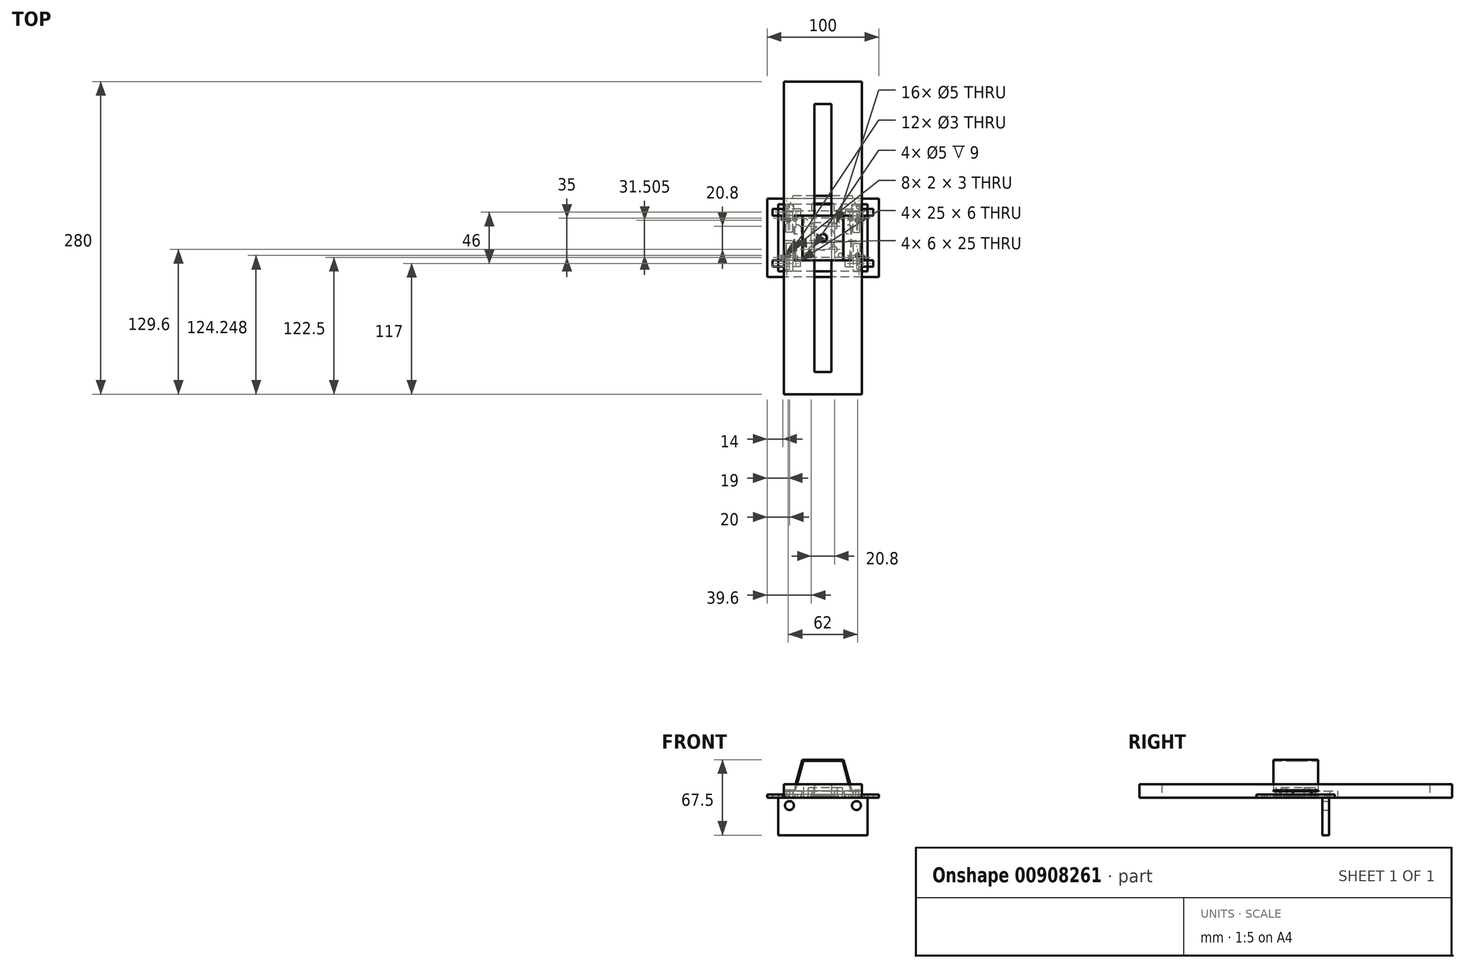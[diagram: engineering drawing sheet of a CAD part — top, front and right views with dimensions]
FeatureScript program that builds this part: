
annotation { "Feature Type Name" : "Feature", "Feature Type Description" : "" }
export const myFeature = defineFeature(function(context is Context, id is Id, definition is map)
    precondition{}
    {
        {
            var Q0;
            Q0=qCreatedBy(makeId("Top.planeOp"),FACE);
            var sketch = newSketch(context, id + "F0", { "sketchPlane" : qUnion([Q0])});
            skLineSegment(sketch, "E0.bottom", {"start": v(40, 30) * mm, "end": v(-40, 30) * mm});
            skLineSegment(sketch, "E0.top", {"start": v(40, -30) * mm, "end": v(-40, -30) * mm});
            skLineSegment(sketch, "E0.left", {"start": v(40, 30) * mm, "end": v(40, -30) * mm});
            skLineSegment(sketch, "E0.right", {"start": v(-40, 30) * mm, "end": v(-40, -30) * mm});
            skPoint(sketch, "E0.middle", {"position": v(0, 0) * mm});
            skCircle(sketch, "E1", {"center": v(0, 0) * mm, "radius": 4.5 * mm});
            skCircle(sketch, "E2", {"center": v(15.5, 15.5) * mm, "radius": 1.75 * mm});
            skCircle(sketch, "E3.MirrorC", {"center": v(-15.5, 15.5) * mm, "radius": 1.75 * mm});
            skCircle(sketch, "E4.MirrorC", {"center": v(-15.5, -15.5) * mm, "radius": 1.75 * mm});
            skCircle(sketch, "E5.MirrorC", {"center": v(15.5, -15.5) * mm, "radius": 1.75 * mm});
            skSolve(sketch);
        }
        {
            var Q0;
            Q0 = qSketchRegion(id + "F0", true);
            extrude(context, id + "F1", {"entities" : qUnion([Q0]), "depth" : 3 * mm, "offsetDistance" : 25 * mm});
        }
        {
            var Q0;
            Q0=makeQuery(id+"F1.opExtrude","CAP_FACE",FACE,{"disambiguationData":[OSD([sQuery(id+"F0.wireOp",EDGE,"E0.bottom"),sQuery(id+"F0.wireOp",EDGE,"E0.top"),sQuery(id+"F0.wireOp",EDGE,"E0.left"),sQuery(id+"F0.wireOp",EDGE,"E0.right"),sQuery(id+"F0.wireOp",EDGE,"E1"),sQuery(id+"F0.wireOp",EDGE,"E2"),sQuery(id+"F0.wireOp",EDGE,"6a0f09f9-d6d8-4e83-8fd7-3011a86620b10.MirrorC"),sQuery(id+"F0.wireOp",EDGE,"6c786a74-0100-4ea5-b8c0-d8c8957705b30.MirrorC"),sQuery(id+"F0.wireOp",EDGE,"6c786a74-0100-4ea5-b8c0-d8c8957705b31.MirrorC")])],"isStart":true});
            var sketch = newSketch(context, id + "F2", { "sketchPlane" : qUnion([Q0])});
            skLineSegment(sketch, "E6.bottom", {"start": v(40, -30) * mm, "end": v(-40, -30) * mm});
            skLineSegment(sketch, "E6.top", {"start": v(40, -24) * mm, "end": v(-40, -24) * mm});
            skLineSegment(sketch, "E6.left", {"start": v(40, -30) * mm, "end": v(40, -24) * mm});
            skLineSegment(sketch, "E6.right", {"start": v(-40, -30) * mm, "end": v(-40, -24) * mm});
            skSolve(sketch);
        }
        {
            var Q0;
            Q0 = qSketchRegion(id + "F2", true);
            extrude(context, id + "F3", {"entities" : qUnion([Q0]), "depth" : 33.5 * mm, "offsetDistance" : 25 * mm});
        }
        {
            var Q0;
            Q0=qCreatedBy(makeId("Top.planeOp"),FACE);
            var sketch = newSketch(context, id + "F4", { "sketchPlane" : qUnion([Q0])});
            skLineSegment(sketch, "E7.bottom", {"start": v(35, 140) * mm, "end": v(-35, 140) * mm});
            skLineSegment(sketch, "E7.top", {"start": v(35, -140) * mm, "end": v(-35, -140) * mm});
            skLineSegment(sketch, "E7.left", {"start": v(35, 140) * mm, "end": v(35, -140) * mm});
            skLineSegment(sketch, "E7.right", {"start": v(-35, 140) * mm, "end": v(-35, -140) * mm});
            skPoint(sketch, "E7.middle", {"position": v(0, 0) * mm});
            skLineSegment(sketch, "E8.bottom", {"start": v(-7.5, 120) * mm, "end": v(7.5, 120) * mm});
            skLineSegment(sketch, "E8.top", {"start": v(-7.5, -120) * mm, "end": v(7.5, -120) * mm});
            skLineSegment(sketch, "E8.left", {"start": v(-7.5, 120) * mm, "end": v(-7.5, -120) * mm});
            skLineSegment(sketch, "E8.right", {"start": v(7.5, 120) * mm, "end": v(7.5, -120) * mm});
            skSolve(sketch);
        }
        {
            var Q0;
            Q0=makeQuery(id+"F4.imprint","IMPRINT",FACE,{"disambiguationData":[TD([[makeQuery(id+"F4.imprint","IMPRINT",EDGE,{"derivedFrom":sQuery(id+"F4.wireOp",EDGE,"E7.bottom")}),1.0]])]});
            extrude(context, id + "F5", {"entities" : qUnion([Q0]), "depth" : 12 * mm, "offsetDistance" : 25 * mm});
        }
        {
            var Q0;
            Q0=makeQuery(id+"F1.opExtrude","CAP_FACE",FACE,{"disambiguationData":[OSD([sQuery(id+"F0.wireOp",EDGE,"E0.bottom"),sQuery(id+"F0.wireOp",EDGE,"E0.top"),sQuery(id+"F0.wireOp",EDGE,"E0.left"),sQuery(id+"F0.wireOp",EDGE,"E0.right"),sQuery(id+"F0.wireOp",EDGE,"E1"),sQuery(id+"F0.wireOp",EDGE,"E2"),sQuery(id+"F0.wireOp",EDGE,"6a0f09f9-d6d8-4e83-8fd7-3011a86620b10.MirrorC"),sQuery(id+"F0.wireOp",EDGE,"6c786a74-0100-4ea5-b8c0-d8c8957705b30.MirrorC"),sQuery(id+"F0.wireOp",EDGE,"6c786a74-0100-4ea5-b8c0-d8c8957705b31.MirrorC")])],"isStart":true});
            var sketch = newSketch(context, id + "F6", { "sketchPlane" : qUnion([Q0])});
            skCircle(sketch, "E9", {"center": v(0, 0) * mm, "radius": 11 * mm});
            skSolve(sketch);
        }
        {
            var Q0;
            Q0 = qSketchRegion(id + "F6", true);
            extrude(context, id + "F7", {"entities" : qUnion([Q0]), "operationType" : NewBodyOperationType.REMOVE, "oppositeDirection" : true, "depth" : 2 * mm, "offsetDistance" : 25 * mm});
        }
        {
            var Q0;
            Q0=makeQuery(id+"F3.boolean.opBoolean","MERGE",FACE,{"derivedFrom":[makeQuery(id+"F1.opExtrude","SWEPT_FACE",FACE,{"disambiguationData":[OSD([sQuery(id+"F0.wireOp",EDGE,"E0.bottom")])]}),makeQuery(id+"F3.opExtrude","SWEPT_FACE",FACE,{"disambiguationData":[OSD([sQuery(id+"F2.wireOp",EDGE,"E6.bottom")])]})]});
            var sketch = newSketch(context, id + "F8", { "sketchPlane" : qUnion([Q0])});
            skCircle(sketch, "E10", {"center": v(-30, -7) * mm, "radius": 4 * mm});
            skCircle(sketch, "E11.MirrorC", {"center": v(30, -7) * mm, "radius": 4 * mm});
            skSolve(sketch);
        }
        {
            var Q0;
            Q0 = qSketchRegion(id + "F8", true);
            extrude(context, id + "F9", {"entities" : qUnion([Q0]), "operationType" : NewBodyOperationType.REMOVE, "oppositeDirection" : true, "depth" : 6 * mm, "offsetDistance" : 25 * mm});
        }
        {
            var Q0;
            Q0=qCreatedBy(makeId("Front.planeOp"),FACE);
            var sketch = newSketch(context, id + "F10", { "sketchPlane" : qUnion([Q0])});
            skLineSegment(sketch, "E12", {"start": v(0, 33) * mm, "end": v(-17.63, 33) * mm});
            skLineSegment(sketch, "E13", {"start": v(-17.63, 33) * mm, "end": v(-25, 5.62) * mm});
            skLineSegment(sketch, "E14", {"start": v(-25, 5.62) * mm, "end": v(-35, 5.62) * mm});
            skLineSegment(sketch, "E15.0", {"start": v(-25.77, 6.62) * mm, "end": v(-35, 6.62) * mm});
            skLineSegment(sketch, "E15.1", {"start": v(-18.4, 34) * mm, "end": v(-25.77, 6.62) * mm});
            skLineSegment(sketch, "E15.2", {"start": v(0, 34) * mm, "end": v(-18.4, 34) * mm});
            skLineSegment(sketch, "E16", {"start": v(-35, 6.62) * mm, "end": v(-35, 5.62) * mm});
            skLineSegment(sketch, "E17.MirrorCS", {"start": v(35, 6.62) * mm, "end": v(35, 5.62) * mm});
            skLineSegment(sketch, "E18.MirrorCS", {"start": v(25, 5.62) * mm, "end": v(35, 5.62) * mm});
            skLineSegment(sketch, "E19.MirrorCS", {"start": v(25.77, 6.62) * mm, "end": v(35, 6.62) * mm});
            skLineSegment(sketch, "E20.MirrorCS", {"start": v(18.4, 34) * mm, "end": v(25.77, 6.62) * mm});
            skLineSegment(sketch, "E21.MirrorCS", {"start": v(17.63, 33) * mm, "end": v(25, 5.62) * mm});
            skLineSegment(sketch, "E22.MirrorCS", {"start": v(0, 34) * mm, "end": v(18.4, 34) * mm});
            skLineSegment(sketch, "E23.MirrorCS", {"start": v(0, 33) * mm, "end": v(17.63, 33) * mm});
            skSolve(sketch);
        }
        {
            var Q0;
            Q0 = qSketchRegion(id + "F10", true);
            extrude(context, id + "F11", {"entities" : qUnion([Q0]), "depth" : 20 * mm, "offsetDistance" : 25 * mm, "hasSecondDirection" : true, "secondDirectionOppositeDirection" : true, "secondDirectionDepth" : 20 * mm});
        }
        {
            var Q0;
            Q0=qCreatedBy(makeId("Top.planeOp"),FACE);
            var sketch = newSketch(context, id + "F12", { "sketchPlane" : qUnion([Q0])});
            skCircle(sketch, "E24", {"center": v(-31, 15.75) * mm, "radius": 1.5 * mm});
            skCircle(sketch, "E25.MirrorC", {"center": v(31, 15.75) * mm, "radius": 1.5 * mm});
            skCircle(sketch, "E26.MirrorC", {"center": v(31, -15.75) * mm, "radius": 1.5 * mm});
            skCircle(sketch, "E27.MirrorC", {"center": v(-31, -15.75) * mm, "radius": 1.5 * mm});
            skSolve(sketch);
        }
        {
            var Q0;
            Q0 = qSketchRegion(id + "F12", true);
            extrude(context, id + "F13", {"entities" : qUnion([Q0]), "operationType" : NewBodyOperationType.REMOVE, "oppositeDirection" : true, "depth" : 25 * mm, "offsetDistance" : 25 * mm, "hasSecondDirection" : true, "secondDirectionOppositeDirection" : false, "secondDirectionDepth" : 25 * mm});
        }
        {
            var Q0;
            Q0=qCreatedBy(makeId("Top.planeOp"),FACE);
            var sketch = newSketch(context, id + "F14", { "sketchPlane" : qUnion([Q0])});
            skCircle(sketch, "E28", {"center": v(0, 0) * mm, "radius": 3.3 * mm});
            skSolve(sketch);
        }
        {
            var Q0;
            Q0 = qSketchRegion(id + "F14", true);
            extrude(context, id + "F15", {"entities" : qUnion([Q0]), "operationType" : NewBodyOperationType.REMOVE, "endBound" : BoundingType.THROUGH_ALL, "depth" : 25 * mm, "offsetDistance" : 25 * mm});
        }
        {
            var Q0;
            Q0=qCreatedBy(makeId("Top.planeOp"),FACE);
            var sketch = newSketch(context, id + "F16", { "sketchPlane" : qUnion([Q0])});
            skLineSegment(sketch, "E29.bottom", {"start": v(50, 35) * mm, "end": v(-50, 35) * mm});
            skLineSegment(sketch, "E29.top", {"start": v(50, -35) * mm, "end": v(-50, -35) * mm});
            skLineSegment(sketch, "E29.left", {"start": v(50, 35) * mm, "end": v(50, -35) * mm});
            skLineSegment(sketch, "E29.right", {"start": v(-50, 35) * mm, "end": v(-50, -35) * mm});
            skPoint(sketch, "E29.middle", {"position": v(0, 0) * mm});
            skLineSegment(sketch, "E30.bottom", {"start": v(27, -5) * mm, "end": v(33, -5) * mm});
            skLineSegment(sketch, "E30.top", {"start": v(27, -30) * mm, "end": v(33, -30) * mm});
            skLineSegment(sketch, "E30.left", {"start": v(27, -5) * mm, "end": v(27, -30) * mm});
            skLineSegment(sketch, "E30.right", {"start": v(33, -5) * mm, "end": v(33, -30) * mm});
            skPoint(sketch, "E30.middle", {"position": v(30, -17.5) * mm});
            skLineSegment(sketch, "E31.MirrorCS", {"start": v(-27, -30) * mm, "end": v(-33, -30) * mm});
            skLineSegment(sketch, "E32.MirrorCS", {"start": v(-33, -5) * mm, "end": v(-33, -30) * mm});
            skLineSegment(sketch, "E33.MirrorCS", {"start": v(-27, -5) * mm, "end": v(-27, -30) * mm});
            skLineSegment(sketch, "E34.MirrorCS", {"start": v(-27, -5) * mm, "end": v(-33, -5) * mm});
            skLineSegment(sketch, "E35.MirrorCS", {"start": v(27, 5) * mm, "end": v(27, 30) * mm});
            skLineSegment(sketch, "E36.MirrorCS", {"start": v(27, 30) * mm, "end": v(33, 30) * mm});
            skLineSegment(sketch, "E37.MirrorCS", {"start": v(27, 5) * mm, "end": v(33, 5) * mm});
            skPoint(sketch, "E38.MirrorP", {"position": v(30, 17.5) * mm});
            skLineSegment(sketch, "E39.MirrorCS", {"start": v(33, 5) * mm, "end": v(33, 30) * mm});
            skLineSegment(sketch, "E40.MirrorCS", {"start": v(-27, 5) * mm, "end": v(-33, 5) * mm});
            skLineSegment(sketch, "E41.MirrorCS", {"start": v(-33, 5) * mm, "end": v(-33, 30) * mm});
            skLineSegment(sketch, "E42.MirrorCS", {"start": v(-27, 5) * mm, "end": v(-27, 30) * mm});
            skLineSegment(sketch, "E43.MirrorCS", {"start": v(-27, 30) * mm, "end": v(-33, 30) * mm});
            skLineSegment(sketch, "E44.bottom", {"start": v(25, -16) * mm, "end": v(23, -16) * mm});
            skLineSegment(sketch, "E44.top", {"start": v(25, -19) * mm, "end": v(23, -19) * mm});
            skLineSegment(sketch, "E44.left", {"start": v(25, -16) * mm, "end": v(25, -19) * mm});
            skLineSegment(sketch, "E44.right", {"start": v(23, -16) * mm, "end": v(23, -19) * mm});
            skPoint(sketch, "E44.middle", {"position": v(24, -17.5) * mm});
            skLineSegment(sketch, "E45", {"start": v(30, -17.5) * mm, "end": v(30, -24.92) * mm, "construction": true});
            skLineSegment(sketch, "E46.MirrorCS", {"start": v(35, -19) * mm, "end": v(37, -19) * mm});
            skLineSegment(sketch, "E47.MirrorCS", {"start": v(35, -16) * mm, "end": v(35, -19) * mm});
            skLineSegment(sketch, "E48.MirrorCS", {"start": v(35, -16) * mm, "end": v(37, -16) * mm});
            skLineSegment(sketch, "E49.MirrorCS", {"start": v(37, -16) * mm, "end": v(37, -19) * mm});
            skLineSegment(sketch, "E50.MirrorCS", {"start": v(-35, -19) * mm, "end": v(-37, -19) * mm});
            skLineSegment(sketch, "E51.MirrorCS", {"start": v(-37, -16) * mm, "end": v(-37, -19) * mm});
            skLineSegment(sketch, "E52.MirrorCS", {"start": v(-35, -16) * mm, "end": v(-37, -16) * mm});
            skLineSegment(sketch, "E53.MirrorCS", {"start": v(-35, -16) * mm, "end": v(-35, -19) * mm});
            skLineSegment(sketch, "E54.MirrorCS", {"start": v(-25, -16) * mm, "end": v(-25, -19) * mm});
            skLineSegment(sketch, "E55.MirrorCS", {"start": v(-25, -19) * mm, "end": v(-23, -19) * mm});
            skLineSegment(sketch, "E56.MirrorCS", {"start": v(-25, -16) * mm, "end": v(-23, -16) * mm});
            skLineSegment(sketch, "E57.MirrorCS", {"start": v(-23, -16) * mm, "end": v(-23, -19) * mm});
            skLineSegment(sketch, "E58.MirrorCS", {"start": v(35, 19) * mm, "end": v(37, 19) * mm});
            skLineSegment(sketch, "E59.MirrorCS", {"start": v(37, 16) * mm, "end": v(37, 19) * mm});
            skLineSegment(sketch, "E60.MirrorCS", {"start": v(35, 16) * mm, "end": v(37, 16) * mm});
            skLineSegment(sketch, "E61.MirrorCS", {"start": v(35, 16) * mm, "end": v(35, 19) * mm});
            skLineSegment(sketch, "E62.MirrorCS", {"start": v(25, 19) * mm, "end": v(23, 19) * mm});
            skLineSegment(sketch, "E63.MirrorCS", {"start": v(23, 16) * mm, "end": v(23, 19) * mm});
            skLineSegment(sketch, "E64.MirrorCS", {"start": v(25, 16) * mm, "end": v(25, 19) * mm});
            skPoint(sketch, "E65.MirrorP", {"position": v(24, 17.5) * mm});
            skLineSegment(sketch, "E66.MirrorCS", {"start": v(25, 16) * mm, "end": v(23, 16) * mm});
            skLineSegment(sketch, "E67.MirrorCS", {"start": v(-25, 16) * mm, "end": v(-23, 16) * mm});
            skLineSegment(sketch, "E68.MirrorCS", {"start": v(-25, 16) * mm, "end": v(-25, 19) * mm});
            skLineSegment(sketch, "E69.MirrorCS", {"start": v(-23, 16) * mm, "end": v(-23, 19) * mm});
            skLineSegment(sketch, "E70.MirrorCS", {"start": v(-25, 19) * mm, "end": v(-23, 19) * mm});
            skLineSegment(sketch, "E71.MirrorCS", {"start": v(-35, 19) * mm, "end": v(-37, 19) * mm});
            skLineSegment(sketch, "E72.MirrorCS", {"start": v(-37, 16) * mm, "end": v(-37, 19) * mm});
            skLineSegment(sketch, "E73.MirrorCS", {"start": v(-35, 16) * mm, "end": v(-37, 16) * mm});
            skLineSegment(sketch, "E74.MirrorCS", {"start": v(-35, 16) * mm, "end": v(-35, 19) * mm});
            skSolve(sketch);
        }
        {
            var Q0;
            Q0 = qSketchRegion(id + "F16", true);
            extrude(context, id + "F17", {"entities" : qUnion([Q0]), "depth" : 3 * mm, "offsetDistance" : 25 * mm});
        }
        {
            var Q0;
            Q0=qCreatedBy(makeId("Top.planeOp"),FACE);
            var sketch = newSketch(context, id + "F18", { "sketchPlane" : qUnion([Q0])});
            skLineSegment(sketch, "E75.bottom", {"start": v(50, 35) * mm, "end": v(-50, 35) * mm});
            skLineSegment(sketch, "E75.top", {"start": v(50, -35) * mm, "end": v(-50, -35) * mm});
            skLineSegment(sketch, "E75.left", {"start": v(50, 35) * mm, "end": v(50, -35) * mm});
            skLineSegment(sketch, "E75.right", {"start": v(-50, 35) * mm, "end": v(-50, -35) * mm});
            skLineSegment(sketch, "E76.bottom", {"start": v(20, 26) * mm, "end": v(45, 26) * mm});
            skLineSegment(sketch, "E76.top", {"start": v(20, 20) * mm, "end": v(45, 20) * mm});
            skLineSegment(sketch, "E76.left", {"start": v(20, 26) * mm, "end": v(20, 20) * mm});
            skLineSegment(sketch, "E76.right", {"start": v(45, 26) * mm, "end": v(45, 20) * mm});
            skLineSegment(sketch, "E77.bottom", {"start": v(34, 28) * mm, "end": v(31, 28) * mm});
            skLineSegment(sketch, "E77.top", {"start": v(34, 30) * mm, "end": v(31, 30) * mm});
            skLineSegment(sketch, "E77.left", {"start": v(34, 28) * mm, "end": v(34, 30) * mm});
            skLineSegment(sketch, "E77.right", {"start": v(31, 28) * mm, "end": v(31, 30) * mm});
            skPoint(sketch, "E77.middle", {"position": v(32.5, 29) * mm});
            skPoint(sketch, "E77.middle.positionSnap0", {"position": v(32.5, 26) * mm});
            skPoint(sketch, "E77.centerSnap0", {"position": v(32.5, 26) * mm});
            skLineSegment(sketch, "E78.bottom", {"start": v(34, 16) * mm, "end": v(31, 16) * mm});
            skLineSegment(sketch, "E78.top", {"start": v(34, 18) * mm, "end": v(31, 18) * mm});
            skLineSegment(sketch, "E78.left", {"start": v(34, 16) * mm, "end": v(34, 18) * mm});
            skLineSegment(sketch, "E78.right", {"start": v(31, 16) * mm, "end": v(31, 18) * mm});
            skPoint(sketch, "E78.middle", {"position": v(32.5, 17) * mm});
            skLineSegment(sketch, "E79.MirrorCS", {"start": v(34, -28) * mm, "end": v(34, -30) * mm});
            skLineSegment(sketch, "E80.MirrorCS", {"start": v(34, -16) * mm, "end": v(34, -18) * mm});
            skLineSegment(sketch, "E81.MirrorCS", {"start": v(31, -28) * mm, "end": v(31, -30) * mm});
            skLineSegment(sketch, "E82.MirrorCS", {"start": v(31, -16) * mm, "end": v(31, -18) * mm});
            skLineSegment(sketch, "E83.MirrorCS", {"start": v(34, -18) * mm, "end": v(31, -18) * mm});
            skLineSegment(sketch, "E84.MirrorCS", {"start": v(34, -30) * mm, "end": v(31, -30) * mm});
            skLineSegment(sketch, "E85.MirrorCS", {"start": v(34, -16) * mm, "end": v(31, -16) * mm});
            skPoint(sketch, "E86.MirrorP", {"position": v(32.5, -26) * mm});
            skLineSegment(sketch, "E87.MirrorCS", {"start": v(34, -28) * mm, "end": v(31, -28) * mm});
            skLineSegment(sketch, "E88.MirrorCS", {"start": v(20, -26) * mm, "end": v(45, -26) * mm});
            skLineSegment(sketch, "E89.MirrorCS", {"start": v(20, -26) * mm, "end": v(20, -20) * mm});
            skLineSegment(sketch, "E90.MirrorCS", {"start": v(45, -26) * mm, "end": v(45, -20) * mm});
            skLineSegment(sketch, "E91.MirrorCS", {"start": v(20, -20) * mm, "end": v(45, -20) * mm});
            skPoint(sketch, "E92.MirrorP", {"position": v(32.5, -17) * mm});
            skPoint(sketch, "E93.MirrorP", {"position": v(32.5, -29) * mm});
            skLineSegment(sketch, "E94.MirrorCS", {"start": v(-31, 16) * mm, "end": v(-31, 18) * mm});
            skLineSegment(sketch, "E95.MirrorCS", {"start": v(-34, 16) * mm, "end": v(-34, 18) * mm});
            skLineSegment(sketch, "E96.MirrorCS", {"start": v(-34, 30) * mm, "end": v(-31, 30) * mm});
            skLineSegment(sketch, "E97.MirrorCS", {"start": v(-34, 28) * mm, "end": v(-31, 28) * mm});
            skLineSegment(sketch, "E98.MirrorCS", {"start": v(-34, -30) * mm, "end": v(-31, -30) * mm});
            skLineSegment(sketch, "E99.MirrorCS", {"start": v(-31, 28) * mm, "end": v(-31, 30) * mm});
            skLineSegment(sketch, "E100.MirrorCS", {"start": v(-34, 18) * mm, "end": v(-31, 18) * mm});
            skLineSegment(sketch, "E101.MirrorCS", {"start": v(-34, -18) * mm, "end": v(-31, -18) * mm});
            skLineSegment(sketch, "E102.MirrorCS", {"start": v(-34, -16) * mm, "end": v(-34, -18) * mm});
            skLineSegment(sketch, "E103.MirrorCS", {"start": v(-31, -16) * mm, "end": v(-31, -18) * mm});
            skLineSegment(sketch, "E104.MirrorCS", {"start": v(-34, 28) * mm, "end": v(-34, 30) * mm});
            skLineSegment(sketch, "E105.MirrorCS", {"start": v(-34, -28) * mm, "end": v(-34, -30) * mm});
            skLineSegment(sketch, "E106.MirrorCS", {"start": v(-31, -28) * mm, "end": v(-31, -30) * mm});
            skLineSegment(sketch, "E107.MirrorCS", {"start": v(-34, -16) * mm, "end": v(-31, -16) * mm});
            skLineSegment(sketch, "E108.MirrorCS", {"start": v(-34, -28) * mm, "end": v(-31, -28) * mm});
            skLineSegment(sketch, "E109.MirrorCS", {"start": v(-34, 16) * mm, "end": v(-31, 16) * mm});
            skPoint(sketch, "E110.MirrorP", {"position": v(-32.5, -26) * mm});
            skPoint(sketch, "E111.MirrorP", {"position": v(-32.5, 26) * mm});
            skLineSegment(sketch, "E112.MirrorCS", {"start": v(-20, -26) * mm, "end": v(-45, -26) * mm});
            skLineSegment(sketch, "E113.MirrorCS", {"start": v(-45, 26) * mm, "end": v(-45, 20) * mm});
            skLineSegment(sketch, "E114.MirrorCS", {"start": v(-20, 20) * mm, "end": v(-45, 20) * mm});
            skPoint(sketch, "E115.MirrorP", {"position": v(-32.5, 29) * mm});
            skLineSegment(sketch, "E116.MirrorCS", {"start": v(-45, -26) * mm, "end": v(-45, -20) * mm});
            skPoint(sketch, "E117.MirrorP", {"position": v(-32.5, -17) * mm});
            skPoint(sketch, "E118.MirrorP", {"position": v(-32.5, -29) * mm});
            skLineSegment(sketch, "E119.MirrorCS", {"start": v(-20, -20) * mm, "end": v(-45, -20) * mm});
            skLineSegment(sketch, "E120.MirrorCS", {"start": v(-20, 26) * mm, "end": v(-20, 20) * mm});
            skLineSegment(sketch, "E121.MirrorCS", {"start": v(-20, -26) * mm, "end": v(-20, -20) * mm});
            skLineSegment(sketch, "E122.MirrorCS", {"start": v(-20, 26) * mm, "end": v(-45, 26) * mm});
            skPoint(sketch, "E123.MirrorP", {"position": v(-32.5, 17) * mm});
            skSolve(sketch);
        }
        {
            var Q0;
            Q0 = qSketchRegion(id + "F18", true);
            var Q1;
            Q1 = qConstructionFilter(qBodyType(qCreatedBy(id + "F18" ,EDGE), BodyType.WIRE), ConstructionObject.NO);
            extrude(context, id + "F19", {"entities" : qUnion([Q0]), "surfaceEntities" : qUnion([Q1]), "depth" : 3 * mm, "offsetDistance" : 25 * mm});
        }
        {
            var Q0;
            Q0=makeQuery(id+"F17.opExtrude","CAP_FACE",FACE,{"disambiguationData":[OSD([sQuery(id+"F16.wireOp",EDGE,"E29.bottom"),sQuery(id+"F16.wireOp",EDGE,"E29.top"),sQuery(id+"F16.wireOp",EDGE,"E29.left"),sQuery(id+"F16.wireOp",EDGE,"E29.right"),sQuery(id+"F16.wireOp",EDGE,"E30.bottom"),sQuery(id+"F16.wireOp",EDGE,"E30.top"),sQuery(id+"F16.wireOp",EDGE,"E30.left"),sQuery(id+"F16.wireOp",EDGE,"E30.right"),sQuery(id+"F16.wireOp",EDGE,"E31.MirrorCS"),sQuery(id+"F16.wireOp",EDGE,"E32.MirrorCS"),sQuery(id+"F16.wireOp",EDGE,"E33.MirrorCS"),sQuery(id+"F16.wireOp",EDGE,"E34.MirrorCS"),sQuery(id+"F16.wireOp",EDGE,"E35.MirrorCS"),sQuery(id+"F16.wireOp",EDGE,"E36.MirrorCS"),sQuery(id+"F16.wireOp",EDGE,"E37.MirrorCS"),sQuery(id+"F16.wireOp",EDGE,"E39.MirrorCS"),sQuery(id+"F16.wireOp",EDGE,"E40.MirrorCS"),sQuery(id+"F16.wireOp",EDGE,"E41.MirrorCS"),sQuery(id+"F16.wireOp",EDGE,"E42.MirrorCS"),sQuery(id+"F16.wireOp",EDGE,"E43.MirrorCS"),sQuery(id+"F16.wireOp",EDGE,"E44.bottom"),sQuery(id+"F16.wireOp",EDGE,"E44.top"),sQuery(id+"F16.wireOp",EDGE,"E44.left"),sQuery(id+"F16.wireOp",EDGE,"E44.right"),sQuery(id+"F16.wireOp",EDGE,"E46.MirrorCS"),sQuery(id+"F16.wireOp",EDGE,"E47.MirrorCS"),sQuery(id+"F16.wireOp",EDGE,"E48.MirrorCS"),sQuery(id+"F16.wireOp",EDGE,"E49.MirrorCS"),sQuery(id+"F16.wireOp",EDGE,"E50.MirrorCS"),sQuery(id+"F16.wireOp",EDGE,"E51.MirrorCS"),sQuery(id+"F16.wireOp",EDGE,"E52.MirrorCS"),sQuery(id+"F16.wireOp",EDGE,"E53.MirrorCS"),sQuery(id+"F16.wireOp",EDGE,"E54.MirrorCS"),sQuery(id+"F16.wireOp",EDGE,"E55.MirrorCS"),sQuery(id+"F16.wireOp",EDGE,"E56.MirrorCS"),sQuery(id+"F16.wireOp",EDGE,"E57.MirrorCS"),sQuery(id+"F16.wireOp",EDGE,"E58.MirrorCS"),sQuery(id+"F16.wireOp",EDGE,"E59.MirrorCS"),sQuery(id+"F16.wireOp",EDGE,"E60.MirrorCS"),sQuery(id+"F16.wireOp",EDGE,"E61.MirrorCS"),sQuery(id+"F16.wireOp",EDGE,"E62.MirrorCS"),sQuery(id+"F16.wireOp",EDGE,"E63.MirrorCS"),sQuery(id+"F16.wireOp",EDGE,"E64.MirrorCS"),sQuery(id+"F16.wireOp",EDGE,"E66.MirrorCS"),sQuery(id+"F16.wireOp",EDGE,"E67.MirrorCS"),sQuery(id+"F16.wireOp",EDGE,"E68.MirrorCS"),sQuery(id+"F16.wireOp",EDGE,"E69.MirrorCS"),sQuery(id+"F16.wireOp",EDGE,"E70.MirrorCS"),sQuery(id+"F16.wireOp",EDGE,"E71.MirrorCS"),sQuery(id+"F16.wireOp",EDGE,"E72.MirrorCS"),sQuery(id+"F16.wireOp",EDGE,"E73.MirrorCS"),sQuery(id+"F16.wireOp",EDGE,"E74.MirrorCS"),sQuery(id+"F16.wireOp",EDGE,"VZndbkfX-qAmE-ZUEq-ywNJ-xfMdwGmCaxmq"),sQuery(id+"F16.wireOp",EDGE,"d38e4950-2861-46fe-aad3-4ece3c017fed0.MirrorC"),sQuery(id+"F16.wireOp",EDGE,"6216d6eb-5774-4c83-a596-fb331fcc54f50.MirrorC"),sQuery(id+"F16.wireOp",EDGE,"6216d6eb-5774-4c83-a596-fb331fcc54f51.MirrorC")])],"isStart":false});
            var sketch = newSketch(context, id + "F20", { "sketchPlane" : qUnion([Q0])});
            skLineSegment(sketch, "E124.bottom", {"start": v(17.5, 17.5) * mm, "end": v(-17.5, 17.5) * mm});
            skLineSegment(sketch, "E124.top", {"start": v(17.5, -17.5) * mm, "end": v(-17.5, -17.5) * mm});
            skLineSegment(sketch, "E124.left", {"start": v(17.5, 17.5) * mm, "end": v(17.5, -17.5) * mm});
            skLineSegment(sketch, "E124.right", {"start": v(-17.5, 17.5) * mm, "end": v(-17.5, -17.5) * mm});
            skPoint(sketch, "E124.middle", {"position": v(0, 0) * mm});
            skSolve(sketch);
        }
        {
            var Q0;
            Q0 = qSketchRegion(id + "F20", true);
            extrude(context, id + "F21", {"entities" : qUnion([Q0]), "depth" : 6 * mm, "offsetDistance" : 25 * mm});
        }
        {
            var Q0;
            Q0=makeQuery(id+"F21.opExtrude","CAP_FACE",FACE,{"disambiguationData":[OSD([sQuery(id+"F20.wireOp",EDGE,"E124.bottom"),sQuery(id+"F20.wireOp",EDGE,"E124.top"),sQuery(id+"F20.wireOp",EDGE,"E124.left"),sQuery(id+"F20.wireOp",EDGE,"E124.right")])],"isStart":false});
            var sketch = newSketch(context, id + "F22", { "sketchPlane" : qUnion([Q0])});
            skCircle(sketch, "E125", {"center": v(10.4, -10.4) * mm, "radius": 2.5 * mm});
            skCircle(sketch, "E126.MirrorC", {"center": v(-10.4, -10.4) * mm, "radius": 2.5 * mm});
            skCircle(sketch, "E127.MirrorC", {"center": v(10.4, 10.4) * mm, "radius": 2.5 * mm});
            skCircle(sketch, "E128.MirrorC", {"center": v(-10.4, 10.4) * mm, "radius": 2.5 * mm});
            skSolve(sketch);
        }
        {
            var Q0;
            Q0 = qSketchRegion(id + "F22", true);
            extrude(context, id + "F23", {"entities" : qUnion([Q0]), "operationType" : NewBodyOperationType.REMOVE, "oppositeDirection" : true, "depth" : 25 * mm, "offsetDistance" : 25 * mm});
        }
        {
            var Q0;
            Q0 = qSketchRegion(id + "F22", true);
            extrude(context, id + "F24", {"entities" : qUnion([Q0]), "operationType" : NewBodyOperationType.REMOVE, "oppositeDirection" : true, "depth" : 25 * mm, "offsetDistance" : 25 * mm});
        }
        {
            var Q0;
            Q0=qCreatedBy(makeId("Top.planeOp"),FACE);
            var sketch = newSketch(context, id + "F25", { "sketchPlane" : qUnion([Q0])});
            skLineSegment(sketch, "E129", {"start": v(-35, -2.5) * mm, "end": v(35, -2.5) * mm});
            skLineSegment(sketch, "E130", {"start": v(-35, -2.5) * mm, "end": v(-35, 14.5) * mm});
            skLineSegment(sketch, "E131", {"start": v(-35, 14.5) * mm, "end": v(-26.59, 37.5) * mm});
            skLineSegment(sketch, "E132", {"start": v(-26.59, 37.5) * mm, "end": v(0, 37.5) * mm});
            skCircle(sketch, "E133", {"center": v(-23, 7.5) * mm, "radius": 4 * mm});
            skCircle(sketch, "E134.MirrorC", {"center": v(23, 7.5) * mm, "radius": 4 * mm});
            skLineSegment(sketch, "E135.MirrorCS", {"start": v(35, -2.5) * mm, "end": v(35, 14.5) * mm});
            skLineSegment(sketch, "E136.MirrorCS", {"start": v(26.59, 37.5) * mm, "end": v(0, 37.5) * mm});
            skLineSegment(sketch, "E137.MirrorCS", {"start": v(35, 14.5) * mm, "end": v(26.59, 37.5) * mm});
            skLineSegment(sketch, "E138.bottom", {"start": v(10, 13.5) * mm, "end": v(-10, 13.5) * mm});
            skLineSegment(sketch, "E138.top", {"start": v(10, 30.5) * mm, "end": v(-10, 30.5) * mm});
            skLineSegment(sketch, "E138.left", {"start": v(10, 13.5) * mm, "end": v(10, 30.5) * mm});
            skLineSegment(sketch, "E138.right", {"start": v(-10, 13.5) * mm, "end": v(-10, 30.5) * mm});
            skPoint(sketch, "E138.middle", {"position": v(0, 22) * mm});
            skSolve(sketch);
        }
        {
            var Q0;
            Q0 = qSketchRegion(id + "F25", true);
            extrude(context, id + "F26", {"entities" : qUnion([Q0]), "depth" : 6 * mm, "offsetDistance" : 25 * mm});
        }
    });
